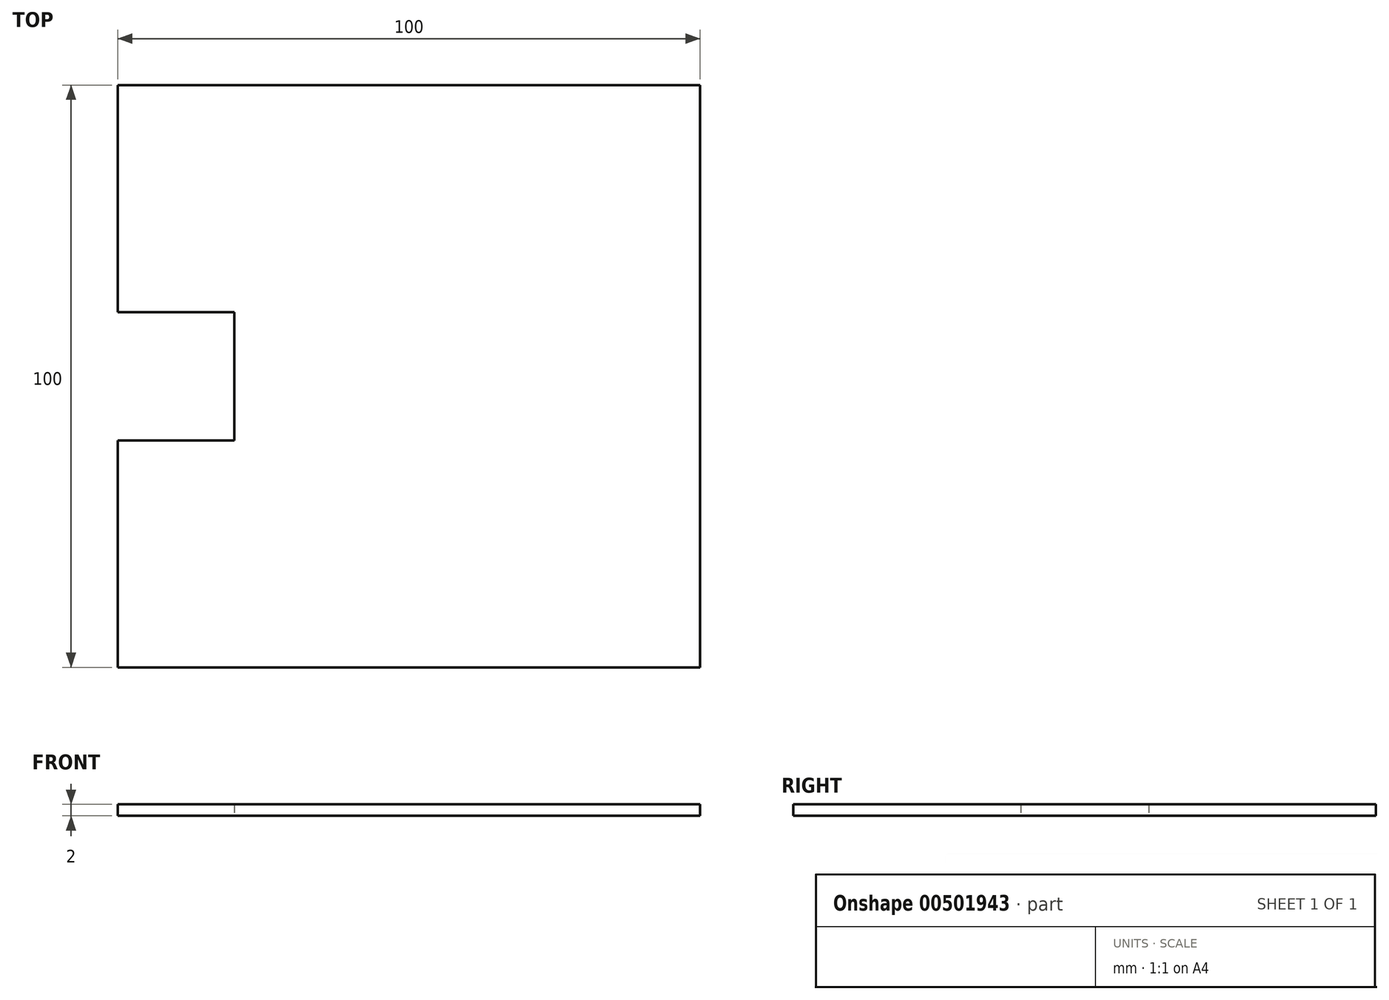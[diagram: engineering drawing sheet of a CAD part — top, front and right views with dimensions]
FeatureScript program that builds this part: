
annotation { "Feature Type Name" : "Feature", "Feature Type Description" : "" }
export const myFeature = defineFeature(function(context is Context, id is Id, definition is map)
    precondition{}
    {
        {
            var Q0;
            Q0=qCreatedBy(makeId("Top.planeOp"),FACE);
            var sketch = newSketch(context, id + "F0", { "sketchPlane" : qUnion([Q0])});
            skLineSegment(sketch, "E0.bottom", {"start": v(50, -50) * mm, "end": v(-50, -50) * mm});
            skLineSegment(sketch, "E0.top", {"start": v(50, 50) * mm, "end": v(-50, 50) * mm});
            skLineSegment(sketch, "E0.left", {"start": v(50, -50) * mm, "end": v(50, 50) * mm});
            skLineSegment(sketch, "E0.right", {"start": v(-50, -50) * mm, "end": v(-50, -11) * mm});
            skPoint(sketch, "E0.middle", {"position": v(0, 0) * mm});
            skLineSegment(sketch, "E1.bottom", {"start": v(-30, -11) * mm, "end": v(-50, -11) * mm});
            skLineSegment(sketch, "E1.top", {"start": v(-30, 11) * mm, "end": v(-50, 11) * mm});
            skLineSegment(sketch, "E1.left", {"start": v(-30, -11) * mm, "end": v(-30, 11) * mm});
            skPoint(sketch, "E1.middle", {"position": v(-50, 0) * mm});
            skPoint(sketch, "E1.right.end.orphan", {"position": v(-70, 11) * mm});
            skPoint(sketch, "E1.right.start.orphan", {"position": v(-70, -11) * mm});
            skLineSegment(sketch, "E2.trimOffspring", {"start": v(-50, 11) * mm, "end": v(-50, 50) * mm});
            skSolve(sketch);
        }
        {
            var Q0;
            Q0=makeQuery(id+"F0.imprint","IMPRINT",FACE,{"disambiguationData":[TD([[makeQuery(id+"F0.imprint","IMPRINT",EDGE,{"derivedFrom":sQuery(id+"F0.wireOp",EDGE,"E0.bottom")}),-1.0]])]});
            extrude(context, id + "F1", {"entities" : qUnion([Q0]), "depth" : 2 * mm, "symmetric" : true});
        }
    });
